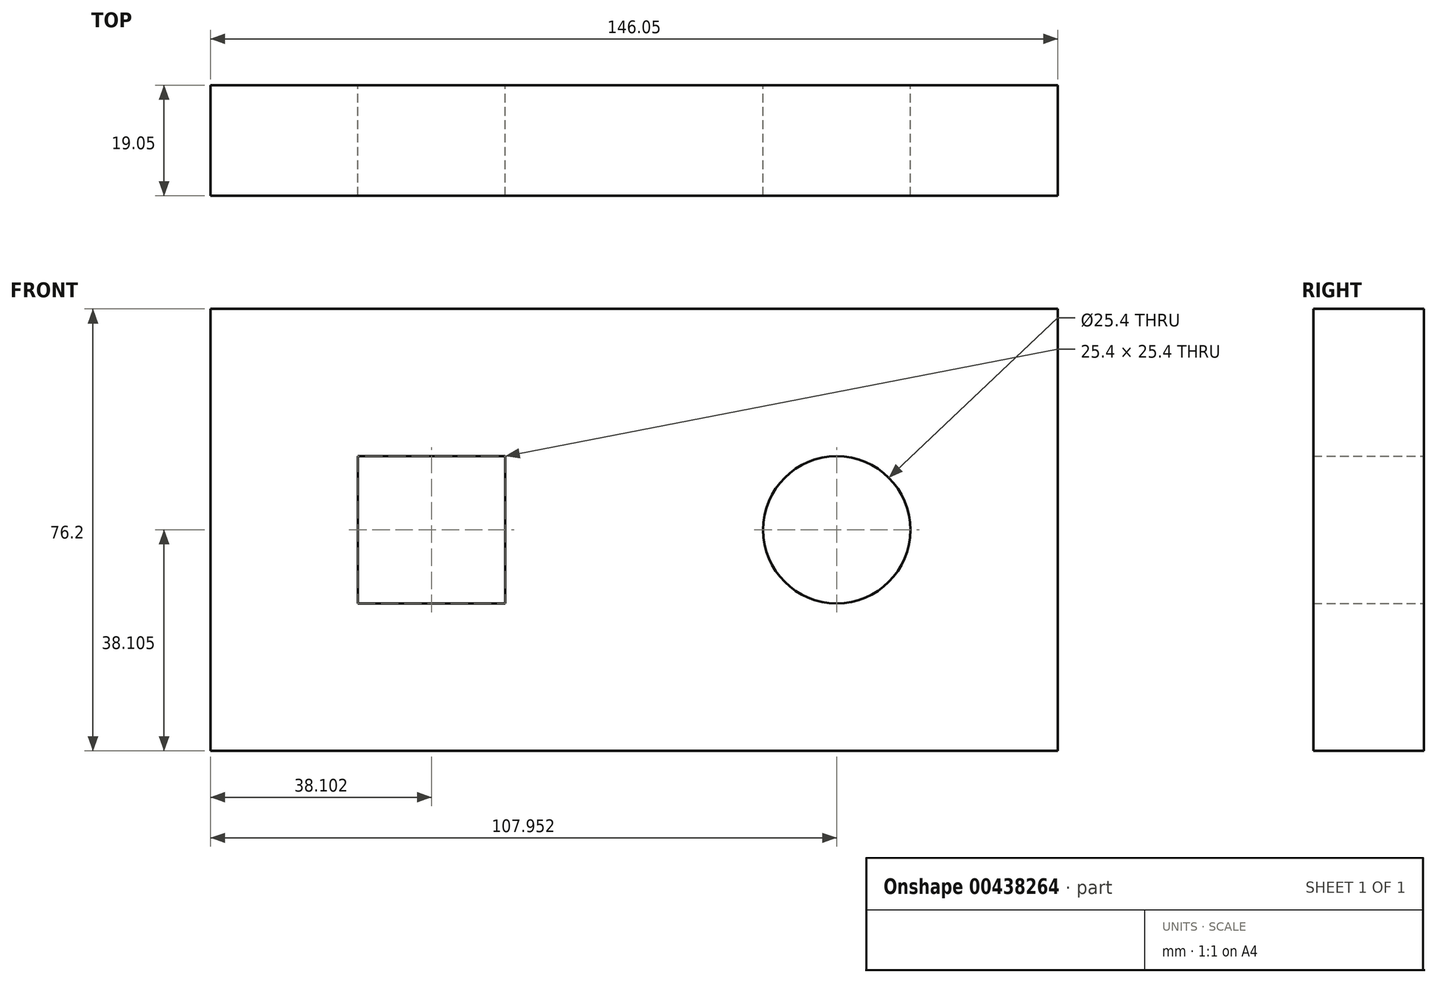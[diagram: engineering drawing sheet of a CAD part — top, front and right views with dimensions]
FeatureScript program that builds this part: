
annotation { "Feature Type Name" : "Feature", "Feature Type Description" : "" }
export const myFeature = defineFeature(function(context is Context, id is Id, definition is map)
    precondition{}
    {
        {
            var Q0;
            Q0=qCreatedBy(makeId("Front.planeOp"),FACE);
            var sketch = newSketch(context, id + "F0", { "sketchPlane" : qUnion([Q0])});
            skLineSegment(sketch, "E0.bottom", {"start": v(87.48, -26.4) * mm, "end": v(-58.57, -26.4) * mm});
            skLineSegment(sketch, "E0.top", {"start": v(87.48, 49.8) * mm, "end": v(-58.57, 49.8) * mm});
            skLineSegment(sketch, "E0.left", {"start": v(87.48, -26.4) * mm, "end": v(87.48, 49.8) * mm});
            skLineSegment(sketch, "E0.right", {"start": v(-58.57, -26.4) * mm, "end": v(-58.57, 49.8) * mm});
            skCircle(sketch, "E1", {"center": v(49.38, 11.7) * mm, "radius": 12.7 * mm});
            skLineSegment(sketch, "E2.bottom", {"start": v(-33.17, 24.4) * mm, "end": v(-7.77, 24.4) * mm});
            skLineSegment(sketch, "E2.top", {"start": v(-33.17, -1) * mm, "end": v(-7.77, -1) * mm});
            skLineSegment(sketch, "E2.left", {"start": v(-33.17, 24.4) * mm, "end": v(-33.17, -1) * mm});
            skLineSegment(sketch, "E2.right", {"start": v(-7.77, 24.4) * mm, "end": v(-7.77, -1) * mm});
            skSolve(sketch);
        }
        {
            var Q0;
            Q0=makeQuery(id+"F0.imprint","IMPRINT",FACE,{"disambiguationData":[TD([[makeQuery(id+"F0.imprint","IMPRINT",EDGE,{"derivedFrom":sQuery(id+"F0.wireOp",EDGE,"E0.bottom")}),-1.0]])]});
            extrude(context, id + "F1", {"entities" : qUnion([Q0]), "depth" : 19.05 * mm});
        }
    });
